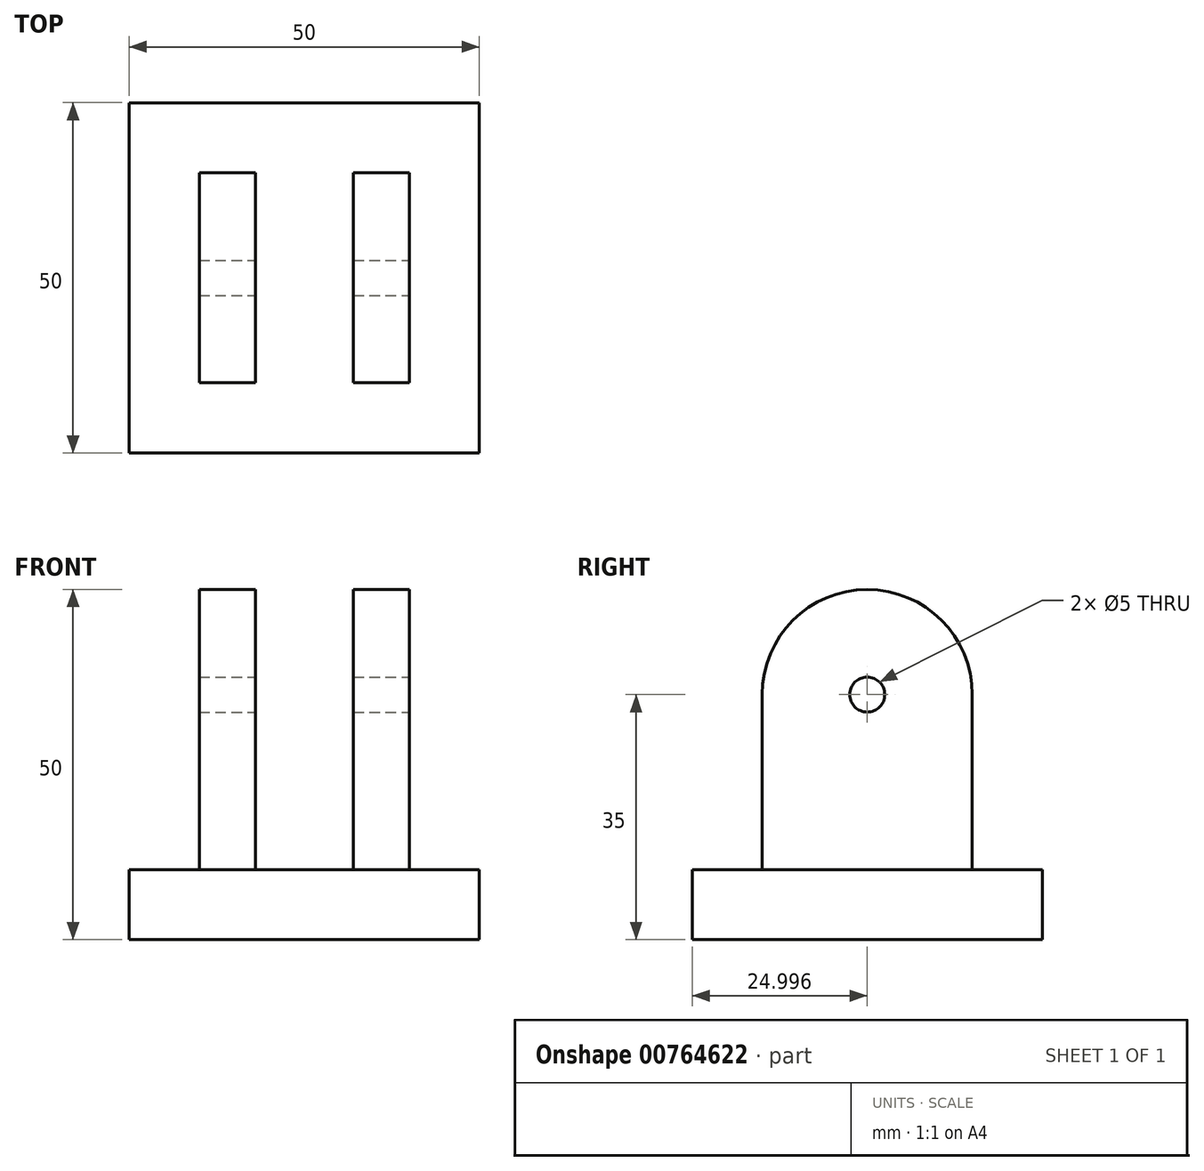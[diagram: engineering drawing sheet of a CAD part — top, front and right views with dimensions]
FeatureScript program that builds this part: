
annotation { "Feature Type Name" : "Feature", "Feature Type Description" : "" }
export const myFeature = defineFeature(function(context is Context, id is Id, definition is map)
    precondition{}
    {
        {
            var Q0;
            Q0=qCreatedBy(makeId("Top.planeOp"),FACE);
            var sketch = newSketch(context, id + "F0", { "sketchPlane" : qUnion([Q0])});
            skLineSegment(sketch, "E0.bottom", {"start": v(-24.12, 28.73) * mm, "end": v(25.88, 28.73) * mm});
            skLineSegment(sketch, "E0.top", {"start": v(-24.12, -21.27) * mm, "end": v(25.88, -21.27) * mm});
            skLineSegment(sketch, "E0.left", {"start": v(-24.12, 28.73) * mm, "end": v(-24.12, -21.27) * mm});
            skLineSegment(sketch, "E0.right", {"start": v(25.88, 28.73) * mm, "end": v(25.88, -21.27) * mm});
            skSolve(sketch);
        }
        {
            var Q0;
            Q0 = qSketchRegion(id + "F0", true);
            extrude(context, id + "F1", {"entities" : qUnion([Q0]), "depth" : 10 * mm, "offsetDistance" : 25 * mm});
        }
        {
            var Q0;
            Q0=makeQuery(id+"F1.opExtrude","CAP_FACE",FACE,{"disambiguationData":[OSD([sQuery(id+"F0.wireOp",EDGE,"E0.bottom"),sQuery(id+"F0.wireOp",EDGE,"E0.top"),sQuery(id+"F0.wireOp",EDGE,"E0.left"),sQuery(id+"F0.wireOp",EDGE,"E0.right")])],"isStart":false});
            var sketch = newSketch(context, id + "F2", { "sketchPlane" : qUnion([Q0])});
            skLineSegment(sketch, "E1.bottom", {"start": v(-14.12, 18.73) * mm, "end": v(-6.12, 18.73) * mm});
            skLineSegment(sketch, "E1.top", {"start": v(-14.12, -11.27) * mm, "end": v(-6.12, -11.27) * mm});
            skLineSegment(sketch, "E1.left", {"start": v(-14.12, 18.73) * mm, "end": v(-14.12, -11.27) * mm});
            skLineSegment(sketch, "E1.right", {"start": v(-6.12, 18.73) * mm, "end": v(-6.12, -11.27) * mm});
            skLineSegment(sketch, "E2.bottom", {"start": v(7.88, 18.73) * mm, "end": v(15.88, 18.73) * mm});
            skLineSegment(sketch, "E2.top", {"start": v(7.88, -11.27) * mm, "end": v(15.88, -11.27) * mm});
            skLineSegment(sketch, "E2.left", {"start": v(7.88, 18.73) * mm, "end": v(7.88, -11.27) * mm});
            skLineSegment(sketch, "E2.right", {"start": v(15.88, 18.73) * mm, "end": v(15.88, -11.27) * mm});
            skSolve(sketch);
        }
        {
            var Q0;
            Q0=makeQuery(id+"F2.imprint","IMPRINT",FACE,{"disambiguationData":[TD([[makeQuery(id+"F2.imprint","IMPRINT",EDGE,{"derivedFrom":sQuery(id+"F2.wireOp",EDGE,"E2.bottom")}),-1.0]])]});
            var Q1;
            Q1=makeQuery(id+"F2.imprint","IMPRINT",FACE,{"disambiguationData":[TD([[makeQuery(id+"F2.imprint","IMPRINT",EDGE,{"derivedFrom":sQuery(id+"F2.wireOp",EDGE,"E1.bottom")}),-1.0]])]});
            extrude(context, id + "F3", {"entities" : qUnion([Q0, Q1]), "operationType" : NewBodyOperationType.ADD, "depth" : 40 * mm, "offsetDistance" : 25 * mm});
        }
        {
            var Q0;
            Q0=makeQuery(id+"F3.opExtrude","CAP_EDGE",EDGE,{"disambiguationData":[OSD([sQuery(id+"F2.wireOp",EDGE,"E1.top")])],"isStart":false});
            var Q1;
            Q1=makeQuery(id+"F3.opExtrude","CAP_EDGE",EDGE,{"disambiguationData":[OSD([sQuery(id+"F2.wireOp",EDGE,"E2.top")])],"isStart":false});
            var Q2;
            Q2=makeQuery(id+"F3.opExtrude","CAP_EDGE",EDGE,{"disambiguationData":[OSD([sQuery(id+"F2.wireOp",EDGE,"E2.bottom")])],"isStart":false});
            var Q3;
            Q3=makeQuery(id+"F3.opExtrude","CAP_EDGE",EDGE,{"disambiguationData":[OSD([sQuery(id+"F2.wireOp",EDGE,"E1.bottom")])],"isStart":false});
            fillet(context, id + "F4", {"entities" : qUnion([Q0, Q1, Q2, Q3]), "radius" : 15 * mm, "tangentPropagation" : true, "allowEdgeOverflow" : false});
        }
        {
            var Q0;
            Q0=makeQuery(id+"F3.opExtrude","SWEPT_FACE",FACE,{"disambiguationData":[OSD([sQuery(id+"F2.wireOp",EDGE,"E2.right")])]});
            var sketch = newSketch(context, id + "F5", { "sketchPlane" : qUnion([Q0])});
            skPoint(sketch, "E3", {"position": v(3.73, 35) * mm});
            skSolve(sketch);
        }
        {
            var Q0;
            Q0=sQuery(id+"F5.wireOp",VERTEX,"E3");
            var Q1;
            Q1=makeQuery(id+"F1.opExtrude","SWEPT_BODY",BODY,{"disambiguationData":[OSD([sQuery(id+"F0.wireOp",EDGE,"E0.bottom"),sQuery(id+"F0.wireOp",EDGE,"E0.top"),sQuery(id+"F0.wireOp",EDGE,"E0.left"),sQuery(id+"F0.wireOp",EDGE,"E0.right")])]});
            hole(context, id + "F6", {"style" : HoleStyle.SIMPLE, "endStyle" : HoleEndStyle.THROUGH, "holeDiameter" : 5 * mm, "majorDiameter" : 5 * mm, "isTappedThrough" : true, "tappedDepth" : 12 * mm, "tapClearance" : 3, "locations" : qUnion([Q0]), "scope" : qUnion([Q1])});
        }
    });
